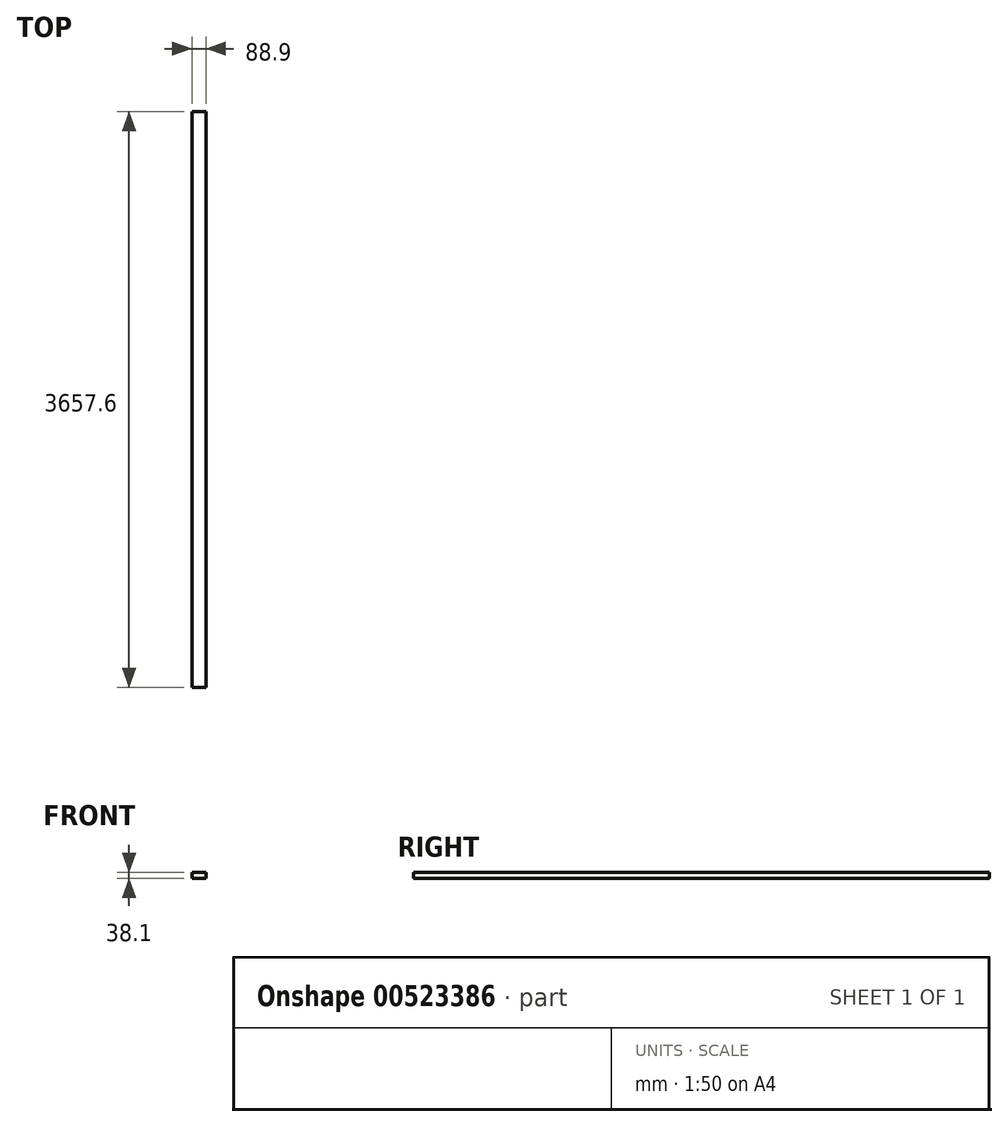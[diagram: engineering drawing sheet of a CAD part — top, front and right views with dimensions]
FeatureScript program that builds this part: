
annotation { "Feature Type Name" : "Feature", "Feature Type Description" : "" }
export const myFeature = defineFeature(function(context is Context, id is Id, definition is map)
    precondition{}
    {
        {
            var Q0;
            Q0=qCreatedBy(makeId("Front.planeOp"),FACE);
            var sketch = newSketch(context, id + "F0", { "sketchPlane" : qUnion([Q0])});
            skLineSegment(sketch, "E0.bottom", {"start": v(44.45, -19.05) * mm, "end": v(-44.45, -19.05) * mm});
            skLineSegment(sketch, "E0.top", {"start": v(44.45, 19.05) * mm, "end": v(-44.45, 19.05) * mm});
            skLineSegment(sketch, "E0.left", {"start": v(44.45, -19.05) * mm, "end": v(44.45, 19.05) * mm});
            skLineSegment(sketch, "E0.right", {"start": v(-44.45, -19.05) * mm, "end": v(-44.45, 19.05) * mm});
            skPoint(sketch, "E0.middle", {"position": v(0, 0) * mm});
            skSolve(sketch);
        }
        {
            var Q0;
            Q0 = qSketchRegion(id + "F0", true);
            extrude(context, id + "F1", {"entities" : qUnion([Q0]), "depth" : 3657.6 * mm, "offsetDistance" : 25.4 * mm});
        }
    });
